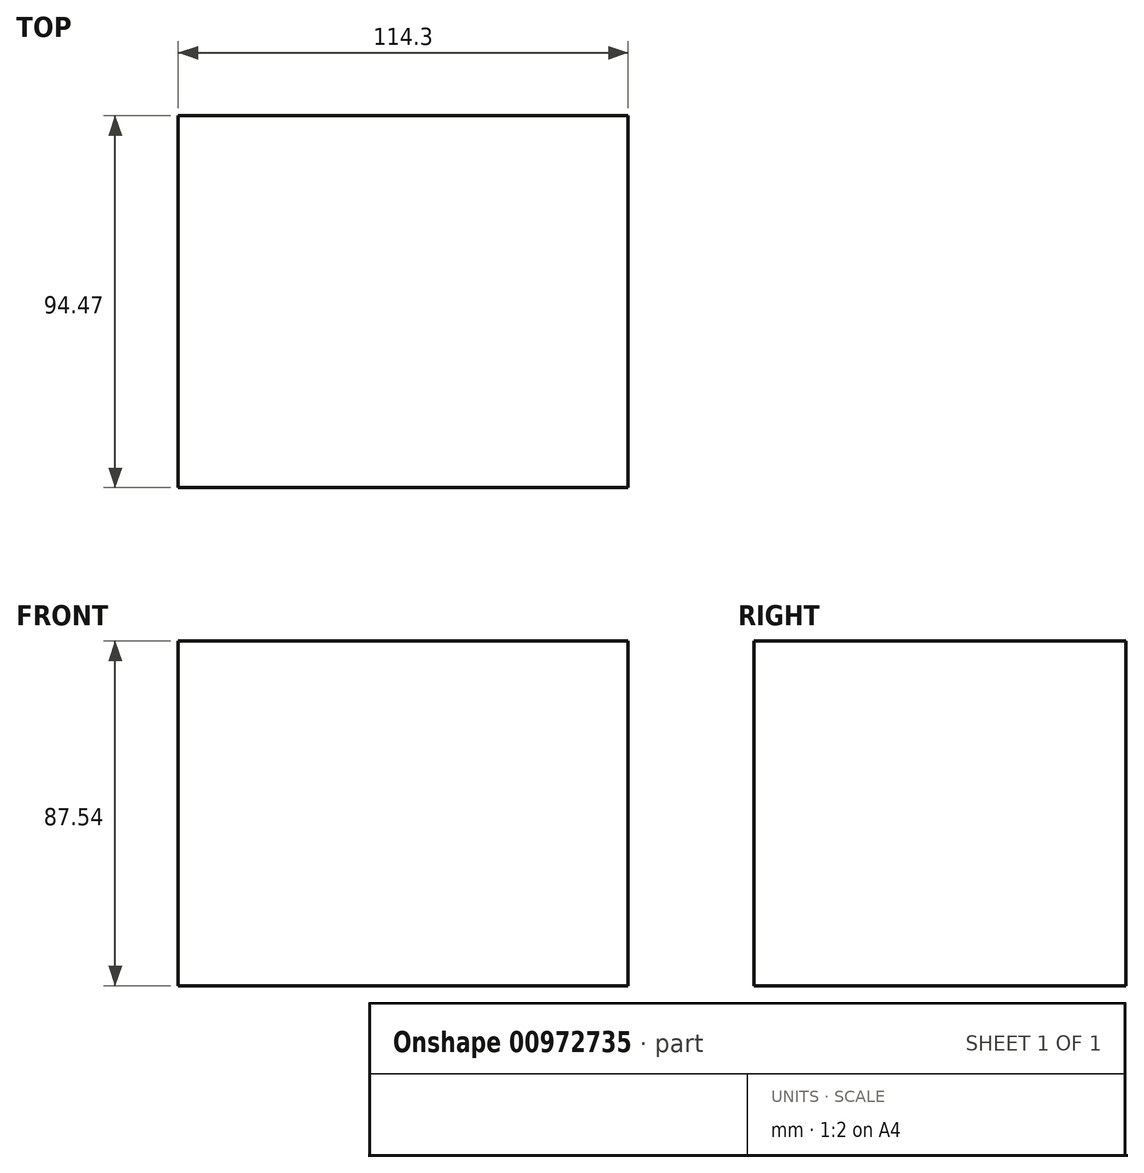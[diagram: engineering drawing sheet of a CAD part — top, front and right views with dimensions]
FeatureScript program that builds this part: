
annotation { "Feature Type Name" : "Feature", "Feature Type Description" : "" }
export const myFeature = defineFeature(function(context is Context, id is Id, definition is map)
    precondition{}
    {
        {
            var Q0;
            Q0=qCreatedBy(makeId("Right.planeOp"),FACE);
            var sketch = newSketch(context, id + "F0", { "sketchPlane" : qUnion([Q0])});
            skLineSegment(sketch, "E0.bottom", {"start": v(-9.38, 40.48) * mm, "end": v(85.1, 40.48) * mm});
            skLineSegment(sketch, "E0.top", {"start": v(-9.38, -47.06) * mm, "end": v(85.1, -47.06) * mm});
            skLineSegment(sketch, "E0.left", {"start": v(-9.38, 40.48) * mm, "end": v(-9.38, -47.06) * mm});
            skLineSegment(sketch, "E0.right", {"start": v(85.1, 40.48) * mm, "end": v(85.1, -47.06) * mm});
            skSolve(sketch);
        }
        {
            var Q0;
            Q0 = qSketchRegion(id + "F0", true);
            extrude(context, id + "F1", {"entities" : qUnion([Q0]), "depth" : 114.3 * mm, "offsetDistance" : 25.4 * mm});
        }
    });
